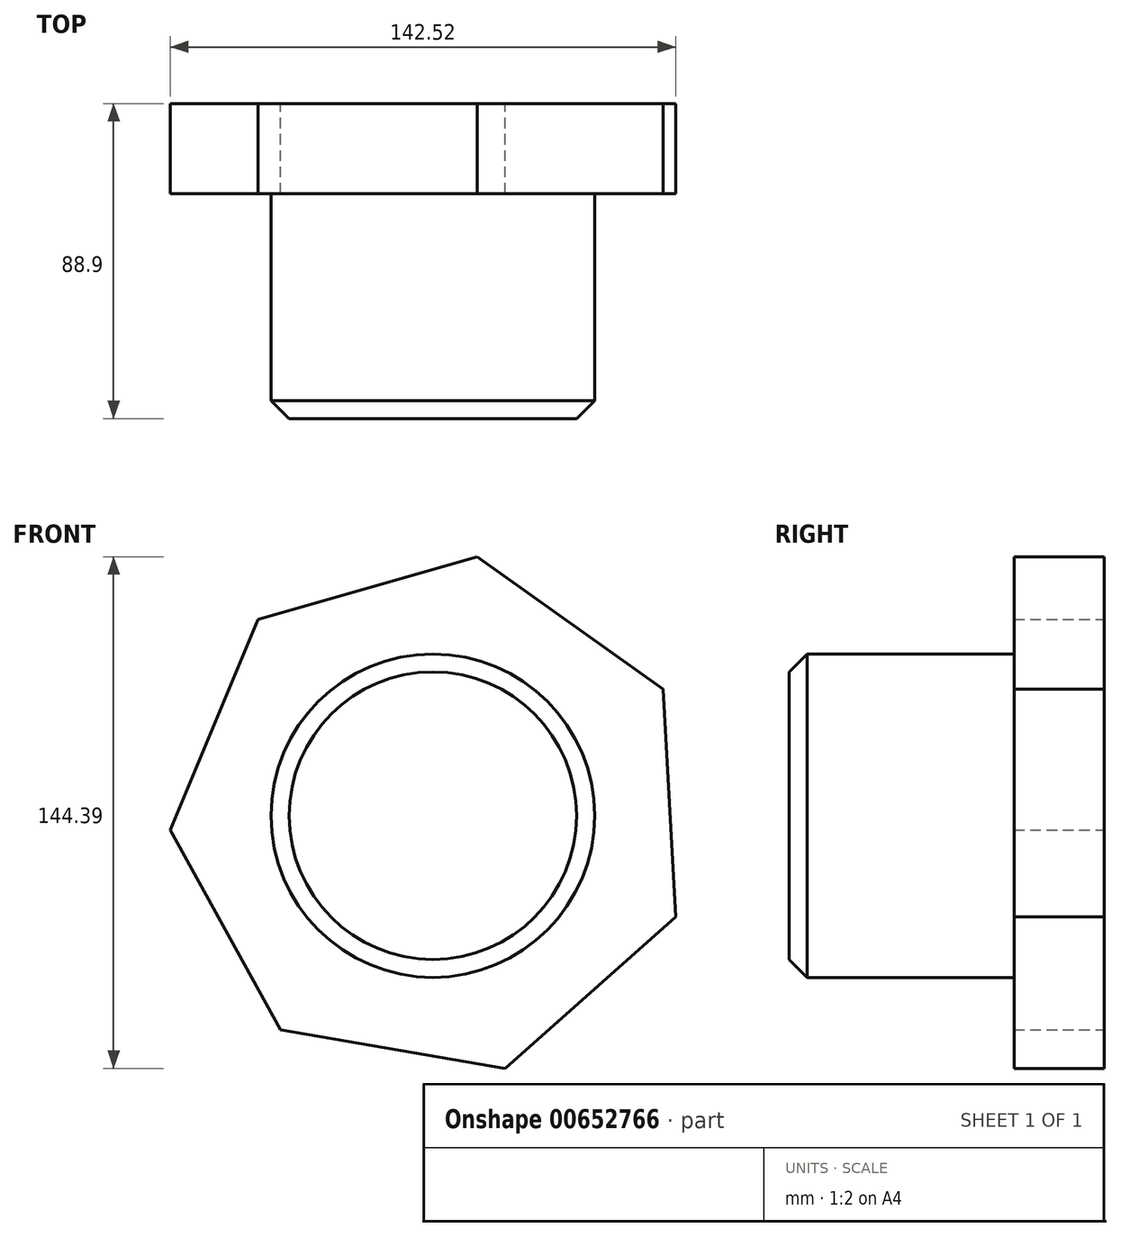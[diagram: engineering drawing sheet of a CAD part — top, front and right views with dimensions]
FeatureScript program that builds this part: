
annotation { "Feature Type Name" : "Feature", "Feature Type Description" : "" }
export const myFeature = defineFeature(function(context is Context, id is Id, definition is map)
    precondition{}
    {
        {
            var Q0;
            Q0=qCreatedBy(makeId("Front.planeOp"),FACE);
            var sketch = newSketch(context, id + "F0", { "sketchPlane" : qUnion([Q0])});
            skCircle(sketch, "E0.cCircle", {"center": v(0, 0) * mm, "radius": 66.82 * mm, "construction": true});
            skLineSegment(sketch, "E0.0", {"start": v(-43, -60.42) * mm, "end": v(-74.05, -4.04) * mm});
            skLineSegment(sketch, "E0.1", {"start": v(-74.05, -4.04) * mm, "end": v(-49.33, 55.38) * mm});
            skLineSegment(sketch, "E0.2", {"start": v(-49.33, 55.38) * mm, "end": v(12.54, 73.1) * mm});
            skLineSegment(sketch, "E0.3", {"start": v(12.54, 73.1) * mm, "end": v(64.96, 35.77) * mm});
            skLineSegment(sketch, "E0.4", {"start": v(64.96, 35.77) * mm, "end": v(68.47, -28.49) * mm});
            skLineSegment(sketch, "E0.5", {"start": v(68.47, -28.49) * mm, "end": v(20.42, -71.3) * mm});
            skLineSegment(sketch, "E0.6", {"start": v(20.42, -71.3) * mm, "end": v(-43, -60.42) * mm});
            skPoint(sketch, "E0.0.midPoint", {"position": v(-58.53, -32.23) * mm});
            skSolve(sketch);
        }
        {
            var Q0;
            Q0 = qSketchRegion(id + "F0", true);
            extrude(context, id + "F1", {"entities" : qUnion([Q0]), "depth" : 25.4 * mm, "offsetDistance" : 25.4 * mm});
        }
        {
            var Q0;
            Q0=makeQuery(id+"F1.opExtrude","CAP_FACE",FACE,{"disambiguationData":[OSD([sQuery(id+"F0.wireOp",EDGE,"E0.0"),sQuery(id+"F0.wireOp",EDGE,"E0.1"),sQuery(id+"F0.wireOp",EDGE,"E0.2"),sQuery(id+"F0.wireOp",EDGE,"E0.3"),sQuery(id+"F0.wireOp",EDGE,"E0.4"),sQuery(id+"F0.wireOp",EDGE,"E0.5"),sQuery(id+"F0.wireOp",EDGE,"E0.6")])],"isStart":false});
            var sketch = newSketch(context, id + "F2", { "sketchPlane" : qUnion([Q0])});
            skCircle(sketch, "E1", {"center": v(0, 0) * mm, "radius": 45.64 * mm});
            skSolve(sketch);
        }
        {
            var Q0;
            Q0=makeQuery(id+"F2.imprint","IMPRINT",FACE,{"disambiguationData":[TD([[makeQuery(id+"F2.imprint","IMPRINT",EDGE,{"derivedFrom":sQuery(id+"F2.wireOp",EDGE,"E1")}),1.0]])]});
            extrude(context, id + "F3", {"entities" : qUnion([Q0]), "operationType" : NewBodyOperationType.ADD, "depth" : 63.5 * mm, "offsetDistance" : 25.4 * mm});
        }
        {
            var Q0;
            Q0=makeQuery(id+"F3.opExtrude","CAP_FACE",FACE,{"disambiguationData":[OSD([sQuery(id+"F2.wireOp",EDGE,"E1")])],"isStart":false});
            chamfer(context, id + "F4", {"entities" : qUnion([Q0]), "width" : 5.08 * mm, "tangentPropagation" : true});
        }
    });
